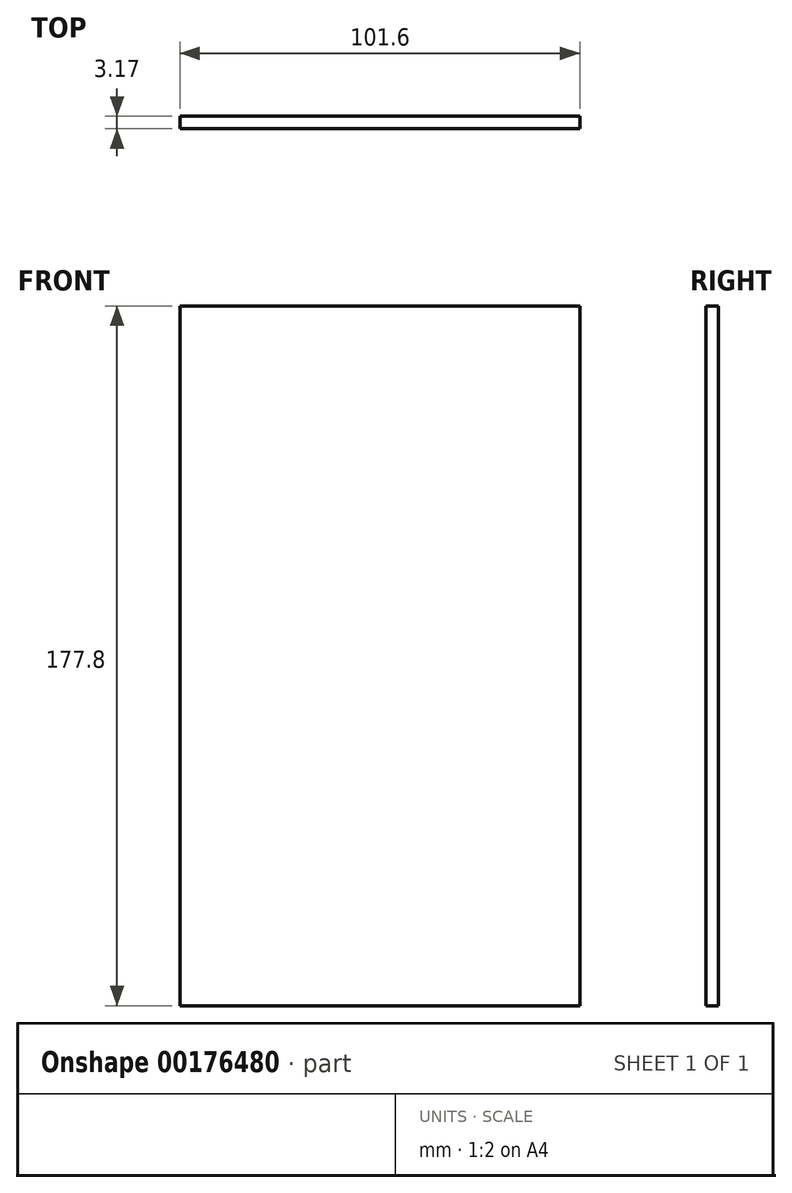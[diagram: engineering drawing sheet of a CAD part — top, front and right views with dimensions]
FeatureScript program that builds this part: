
annotation { "Feature Type Name" : "Feature", "Feature Type Description" : "" }
export const myFeature = defineFeature(function(context is Context, id is Id, definition is map)
    precondition{}
    {
        {
            var Q0;
            Q0=qCreatedBy(makeId("Front.planeOp"),FACE);
            var sketch = newSketch(context, id + "F0", { "sketchPlane" : qUnion([Q0])});
            skLineSegment(sketch, "E0.bottom", {"start": v(-50.08, -54.7) * mm, "end": v(51.52, -54.7) * mm});
            skLineSegment(sketch, "E0.top", {"start": v(-50.08, 123.1) * mm, "end": v(51.52, 123.1) * mm});
            skLineSegment(sketch, "E0.left", {"start": v(-50.08, -54.7) * mm, "end": v(-50.08, 123.1) * mm});
            skLineSegment(sketch, "E0.right", {"start": v(51.52, -54.7) * mm, "end": v(51.52, 123.1) * mm});
            skSolve(sketch);
        }
        {
            var Q0;
            Q0=makeQuery(id+"F0.imprint","IMPRINT",FACE,{"disambiguationData":[TD([[makeQuery(id+"F0.imprint","IMPRINT",EDGE,{"derivedFrom":sQuery(id+"F0.wireOp",EDGE,"E0.bottom")}),1.0]])]});
            extrude(context, id + "F1", {"entities" : qUnion([Q0]), "depth" : 3.17 * mm});
        }
    });
